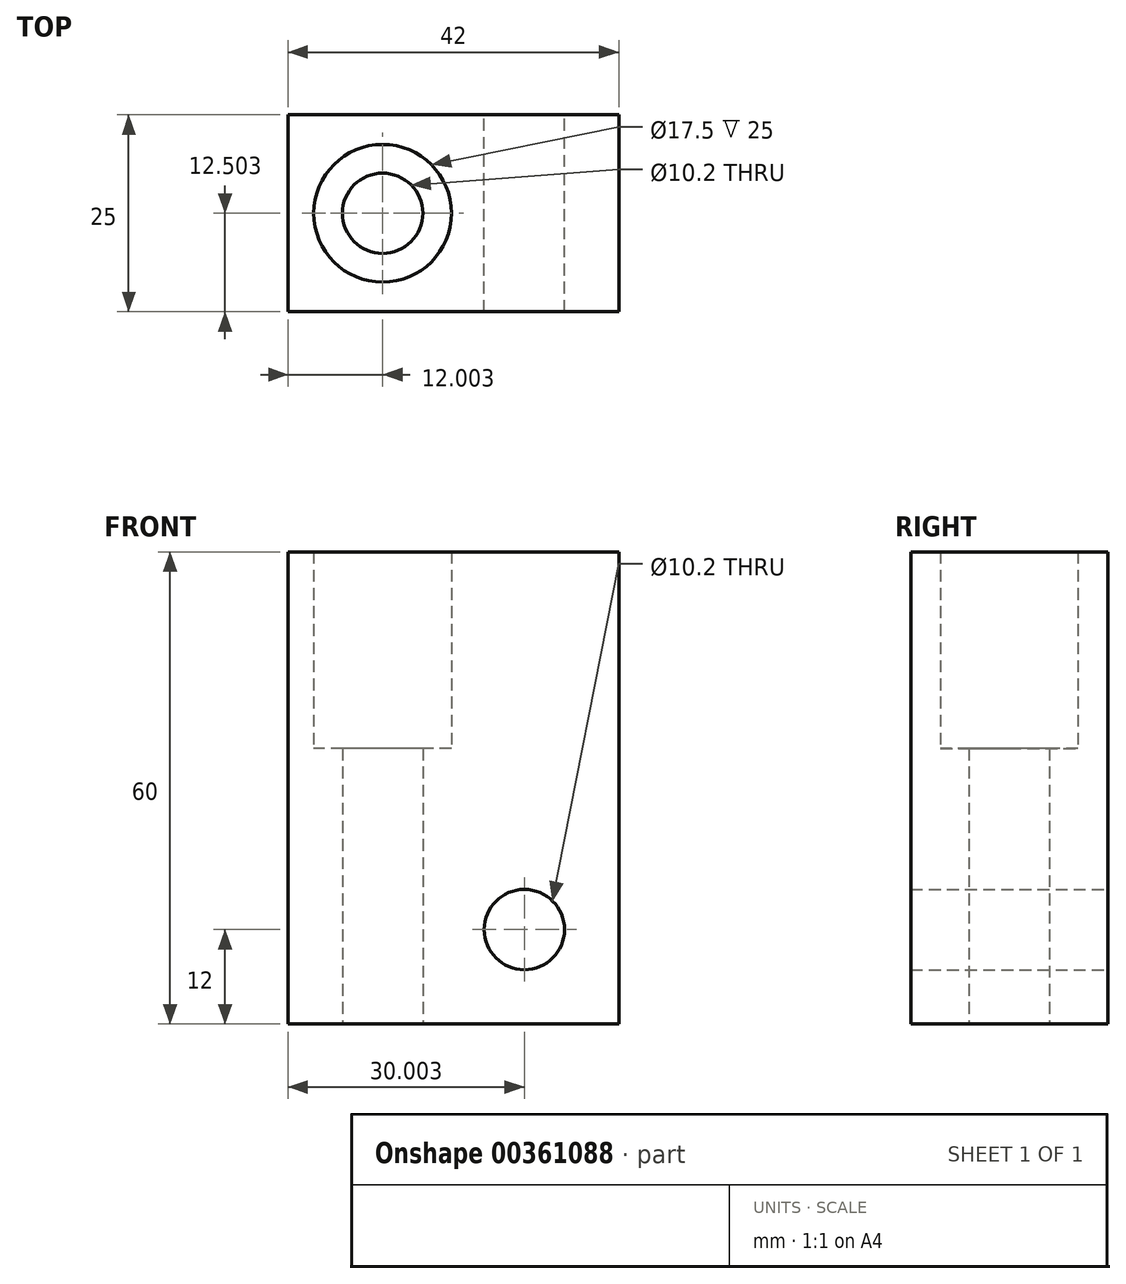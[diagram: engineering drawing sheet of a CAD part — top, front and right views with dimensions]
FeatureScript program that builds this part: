
annotation { "Feature Type Name" : "Feature", "Feature Type Description" : "" }
export const myFeature = defineFeature(function(context is Context, id is Id, definition is map)
    precondition{}
    {
        {
            var Q0;
            Q0=qCreatedBy(makeId("Top.planeOp"),FACE);
            var sketch = newSketch(context, id + "F0", { "sketchPlane" : qUnion([Q0])});
            skLineSegment(sketch, "E0", {"start": v(-23.66, -39.74) * mm, "end": v(18.34, -39.74) * mm});
            skLineSegment(sketch, "E1", {"start": v(18.34, -39.74) * mm, "end": v(18.34, -14.74) * mm});
            skLineSegment(sketch, "E2", {"start": v(18.34, -14.74) * mm, "end": v(-23.66, -14.74) * mm});
            skLineSegment(sketch, "E3", {"start": v(-23.66, -14.74) * mm, "end": v(-23.66, -39.74) * mm});
            skCircle(sketch, "E4", {"center": v(-11.66, -27.24) * mm, "radius": 5.1 * mm});
            skCircle(sketch, "E5", {"center": v(-11.66, -27.24) * mm, "radius": 8.75 * mm});
            skSolve(sketch);
        }
        {
            var Q0;
            Q0=makeQuery(id+"F0.imprint","IMPRINT",FACE,{"disambiguationData":[TD([[makeQuery(id+"F0.imprint","IMPRINT",EDGE,{"derivedFrom":sQuery(id+"F0.wireOp",EDGE,"E0")}),1.0]])]});
            extrude(context, id + "F1", {"entities" : qUnion([Q0]), "depth" : 60 * mm});
        }
        {
            var Q0;
            Q0=makeQuery(id+"F0.imprint","IMPRINT",FACE,{"disambiguationData":[TD([[makeQuery(id+"F0.imprint","IMPRINT",EDGE,{"derivedFrom":sQuery(id+"F0.wireOp",EDGE,"E4")}),-1.0]])]});
            extrude(context, id + "F2", {"entities" : qUnion([Q0]), "operationType" : NewBodyOperationType.ADD, "depth" : 35 * mm});
        }
        {
            var Q0;
            Q0=makeQuery(id+"F1.opExtrude","SWEPT_FACE",FACE,{"disambiguationData":[OSD([sQuery(id+"F0.wireOp",EDGE,"E2")])]});
            var sketch = newSketch(context, id + "F3", { "sketchPlane" : qUnion([Q0])});
            skCircle(sketch, "E6", {"center": v(-6.34, 12) * mm, "radius": 5.1 * mm});
            skPoint(sketch, "E7.end.orphan", {"position": v(-6.34, 0) * mm});
            skPoint(sketch, "E8.end.orphan", {"position": v(-18.34, 12) * mm});
            skSolve(sketch);
        }
        {
            var Q0;
            Q0=makeQuery(id+"F3.imprint","IMPRINT",FACE,{"disambiguationData":[TD([[makeQuery(id+"F3.imprint","IMPRINT",EDGE,{"derivedFrom":sQuery(id+"F3.wireOp",EDGE,"E6")}),1.0]])]});
            extrude(context, id + "F4", {"entities" : qUnion([Q0]), "operationType" : NewBodyOperationType.REMOVE, "oppositeDirection" : true, "depth" : 47.6 * mm});
        }
    });
